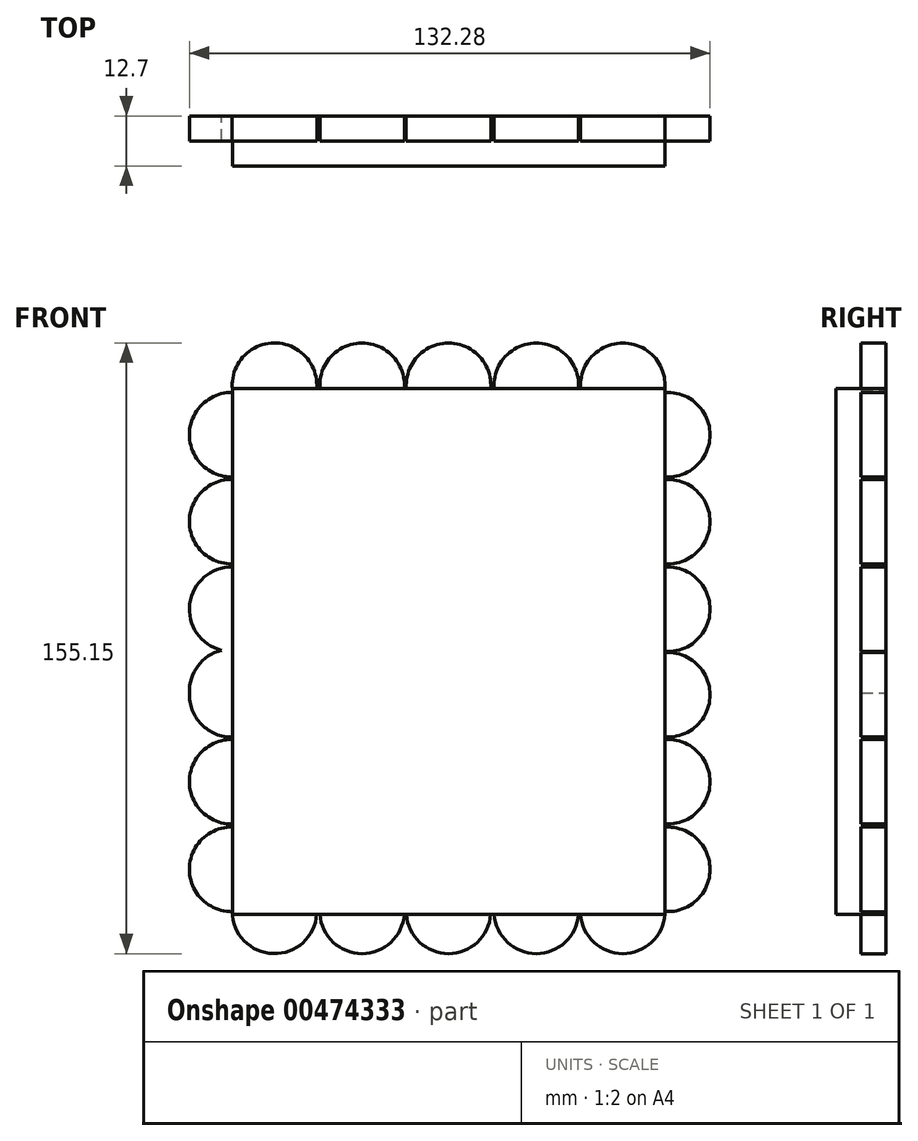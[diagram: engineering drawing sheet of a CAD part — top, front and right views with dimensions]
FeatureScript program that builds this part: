
annotation { "Feature Type Name" : "Feature", "Feature Type Description" : "" }
export const myFeature = defineFeature(function(context is Context, id is Id, definition is map)
    precondition{}
    {
        {
            var Q0;
            Q0=qCreatedBy(makeId("Front.planeOp"),FACE);
            var sketch = newSketch(context, id + "F0", { "sketchPlane" : qUnion([Q0])});
            skLineSegment(sketch, "E0.bottom", {"start": v(54.96, 66.8) * mm, "end": v(-54.96, 66.8) * mm});
            skLineSegment(sketch, "E0.top", {"start": v(54.96, -66.8) * mm, "end": v(-54.96, -66.8) * mm});
            skLineSegment(sketch, "E0.left", {"start": v(54.96, 66.8) * mm, "end": v(54.96, -66.8) * mm});
            skLineSegment(sketch, "E0.right", {"start": v(-54.96, 66.8) * mm, "end": v(-54.96, -66.8) * mm});
            skPoint(sketch, "E0.middle", {"position": v(0, 0) * mm});
            skSolve(sketch);
        }
        {
            var Q0;
            Q0=makeQuery(id+"F0.imprint","IMPRINT",FACE,{"disambiguationData":[TD([[makeQuery(id+"F0.imprint","IMPRINT",EDGE,{"derivedFrom":sQuery(id+"F0.wireOp",EDGE,"E0.bottom")}),1.0]])]});
            extrude(context, id + "F1", {"entities" : qUnion([Q0]), "depth" : 12.7 * mm});
        }
        {
            var Q0;
            Q0=qCreatedBy(makeId("Front.planeOp"),FACE);
            var sketch = newSketch(context, id + "F2", { "sketchPlane" : qUnion([Q0])});
            skCircle(sketch, "E1", {"center": v(-55.16, 55.03) * mm, "radius": 10.74 * mm});
            skCircle(sketch, "E2", {"center": v(-55.16, 32.96) * mm, "radius": 10.74 * mm});
            skCircle(sketch, "E3", {"center": v(-55.16, 10.7) * mm, "radius": 10.74 * mm});
            skCircle(sketch, "E4", {"center": v(-55.16, -10.16) * mm, "radius": 10.74 * mm});
            skCircle(sketch, "E5", {"center": v(-55.16, -11.05) * mm, "radius": 10.74 * mm});
            skCircle(sketch, "E6", {"center": v(-55.16, -33.13) * mm, "radius": 10.74 * mm});
            skCircle(sketch, "E7", {"center": v(-55.16, -55.39) * mm, "radius": 10.74 * mm});
            skCircle(sketch, "E8", {"center": v(55.63, 55.03) * mm, "radius": 10.74 * mm});
            skCircle(sketch, "E9", {"center": v(55.63, 32.96) * mm, "radius": 10.74 * mm});
            skCircle(sketch, "E10", {"center": v(55.63, 10.7) * mm, "radius": 10.74 * mm});
            skCircle(sketch, "E11", {"center": v(55.63, -11.05) * mm, "radius": 10.74 * mm});
            skCircle(sketch, "E12", {"center": v(55.63, -33.13) * mm, "radius": 10.74 * mm});
            skCircle(sketch, "E13", {"center": v(55.63, -55.39) * mm, "radius": 10.74 * mm});
            skCircle(sketch, "E14", {"center": v(44.2, 67.6) * mm, "radius": 10.74 * mm});
            skCircle(sketch, "E15", {"center": v(22.24, 67.6) * mm, "radius": 10.74 * mm});
            skCircle(sketch, "E16", {"center": v(-0.07, 67.6) * mm, "radius": 10.74 * mm});
            skCircle(sketch, "E17", {"center": v(-22.03, 67.6) * mm, "radius": 10.74 * mm});
            skCircle(sketch, "E18", {"center": v(-44.28, 67.6) * mm, "radius": 10.74 * mm});
            skCircle(sketch, "E19", {"center": v(44.2, -66.06) * mm, "radius": 10.74 * mm});
            skCircle(sketch, "E20", {"center": v(22.24, -66.06) * mm, "radius": 10.74 * mm});
            skCircle(sketch, "E21", {"center": v(-0.07, -66.06) * mm, "radius": 10.74 * mm});
            skCircle(sketch, "E22", {"center": v(-22.03, -66.06) * mm, "radius": 10.74 * mm});
            skCircle(sketch, "E23", {"center": v(-44.28, -66.06) * mm, "radius": 10.74 * mm});
            skSolve(sketch);
        }
        {
            var Q0;
            Q0 = qSketchRegion(id + "F2", true);
            extrude(context, id + "F3", {"entities" : qUnion([Q0]), "operationType" : NewBodyOperationType.ADD, "depth" : 6.35 * mm});
        }
    });
